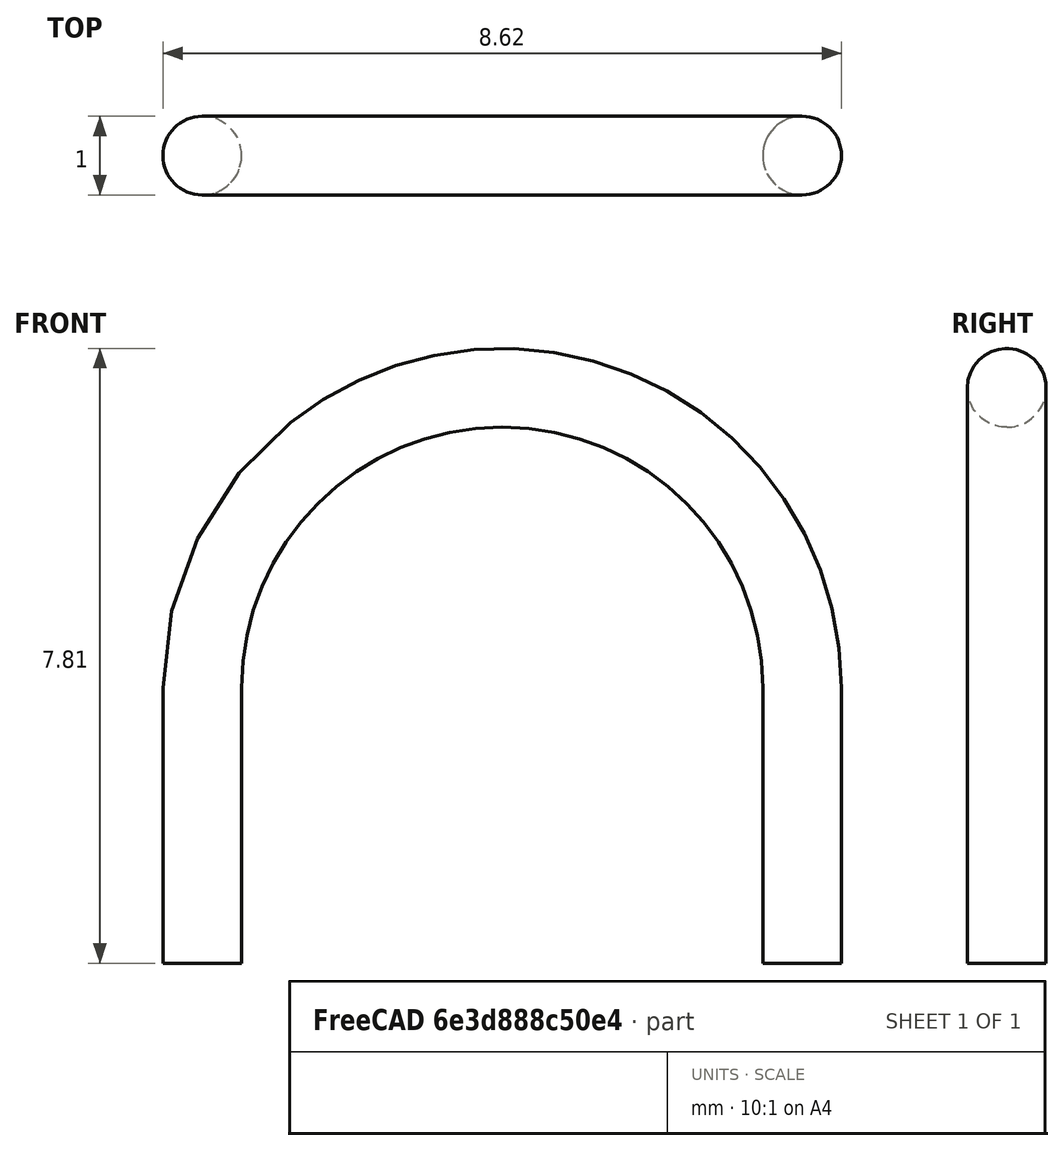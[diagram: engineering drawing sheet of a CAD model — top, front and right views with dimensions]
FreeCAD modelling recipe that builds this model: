
FCSTD DOCUMENT  (FreeCAD 0.17R12018 (Git))
Label: Test_Point_Bridge_Pitch7.62mm_Drill1.3mm
License: All rights reserved
LicenseURL: http://en.wikipedia.org/wiki/All_rights_reserved
objects: Sketcher::SketchObject×2, Spreadsheet::Sheet×1, PartDesign::SubtractivePipe×1, PartDesign::Body×1
note: 5 computed .brp shape members not serialized (recipe doc carries the construction recipe); baked Part::Feature solids carry a one-line shape summary decoded from their .brp

FEATURE [Sketcher::SketchObject] Sketch
  MapMode = 5
  Placement = pos=(0,0,-3) rot=(0,0,1;0rad)
  Support = -> [XY_Plane]
  superPlacement = pos=(0,0,-3) rot=(0,0,1;0rad)
  expr: Constraints[1] = dims.DWire / 2
  sketch-geometry (1):
    g0: Circle CenterX=0 CenterY=0 CenterZ=0 NormalX=0 NormalY=0 NormalZ=1 Radius=0.5
  constraints (2):
    c: Coincident(g0,g-1)
    c: Radius(g0) = 0.5
FEATURE [Spreadsheet::Sheet] Spreadsheet  label="dims"
  cells = A1="DWire"; B1(DWire)=1; A2="Pitch"; B2(Pitch)=7.6200000000000001
FEATURE [Sketcher::SketchObject] Sketch001
  MapMode = 5
  Placement = pos=(0,0,0) rot=(1,0,0;1.5708rad)
  Support = -> [XZ_Plane]
  expr: Constraints[10] = dims.DWire / 2
  expr: Constraints[3] = dims.Pitch
  sketch-geometry (4):
    g0: LineSegment StartX=0 StartY=-3 StartZ=0 EndX=0 EndY=0.5 EndZ=0
    g1: LineSegment StartX=7.62 StartY=0.5 StartZ=0 EndX=7.62 EndY=-3 EndZ=0
    g2: LineSegment [constr] StartX=0 StartY=0.5 StartZ=0 EndX=7.62 EndY=0.5 EndZ=0
    g3: ArcOfCircle CenterX=3.81 CenterY=0.5 CenterZ=0 NormalX=0 NormalY=0 NormalZ=1 Radius=3.81 StartAngle=0 EndAngle=3.14159
  constraints (13):
    c: PointOnObject(g0,g-2)
    c: Vertical(g0)
    c: Vertical(g1)
    c: DistanceX(g0,g1) = 7.62
    c: Coincident(g2,g0)
    c: Coincident(g2,g1)
    c: Horizontal(g2)
    c: PointOnObject(g3,g2)
    c: Coincident(g3,g0)
    c: Coincident(g3,g1)
    c: DistanceY(g-1,g3) = 0.5
    c: DistanceY(g0,g-1) = 3
    c: Equal(g1,g0)
FEATURE [PartDesign::SubtractivePipe] SubtractivePipe
  AuxilleryCurvelinear = true
  AuxillerySpineTangent = false
  Binormal = (0,0,0)
  Mode = 0
  Profile = -> Sketch
  Spine = -> Sketch001
  SpineTangent = false
  Transformation = 0
  Transition = 0
FEATURE [PartDesign::Body] Body  label="Test_Point_Bridge_Pitch7.62mm_Drill1.3mm"
  Group = -> [Sketch,Sketch001,SubtractivePipe]
  Origin = -> Origin
  Tip = -> SubtractivePipe
